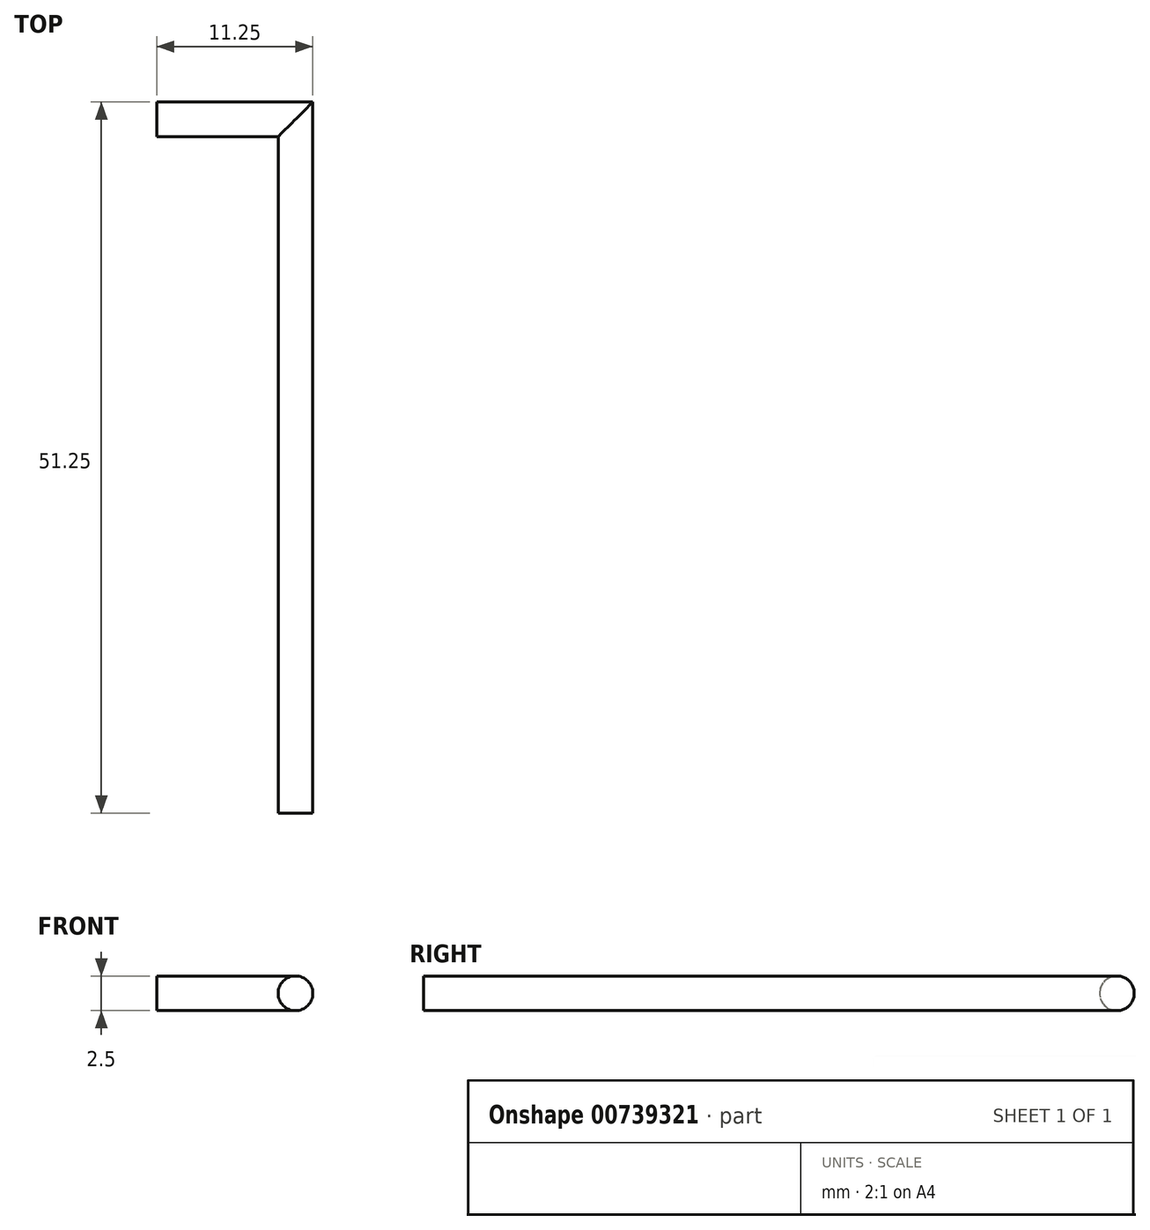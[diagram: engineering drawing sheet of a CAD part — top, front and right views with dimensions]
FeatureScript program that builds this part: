
annotation { "Feature Type Name" : "Feature", "Feature Type Description" : "" }
export const myFeature = defineFeature(function(context is Context, id is Id, definition is map)
    precondition{}
    {
        {
            var Q0;
            Q0=qCreatedBy(makeId("Top.planeOp"),FACE);
            var sketch = newSketch(context, id + "F0", { "sketchPlane" : qUnion([Q0])});
            skLineSegment(sketch, "E0", {"start": v(0, 0) * mm, "end": v(10, 0) * mm});
            skLineSegment(sketch, "E1", {"start": v(10, 0) * mm, "end": v(10, -50) * mm});
            skSolve(sketch);
        }
        {
            var Q0;
            Q0=qCreatedBy(makeId("Right.planeOp"),FACE);
            var sketch = newSketch(context, id + "F1", { "sketchPlane" : qUnion([Q0])});
            skCircle(sketch, "E2", {"center": v(0, 0) * mm, "radius": 1.25 * mm});
            skSolve(sketch);
        }
        {
            var Q0;
            Q0=makeQuery(id+"F1.imprint","IMPRINT",FACE,{"disambiguationData":[TD([[makeQuery(id+"F1.imprint","IMPRINT",EDGE,{"derivedFrom":sQuery(id+"F1.wireOp",EDGE,"E2")}),1.0]])]});
            var Q1;
            Q1=sQuery(id+"F0.wireOp",EDGE,"E0");
            var Q2;
            Q2=sQuery(id+"F0.wireOp",EDGE,"E1");
            sweep(context, id + "F2", {"profiles" : qUnion([Q0]), "path" : qUnion([Q1, Q2])});
        }
    });
